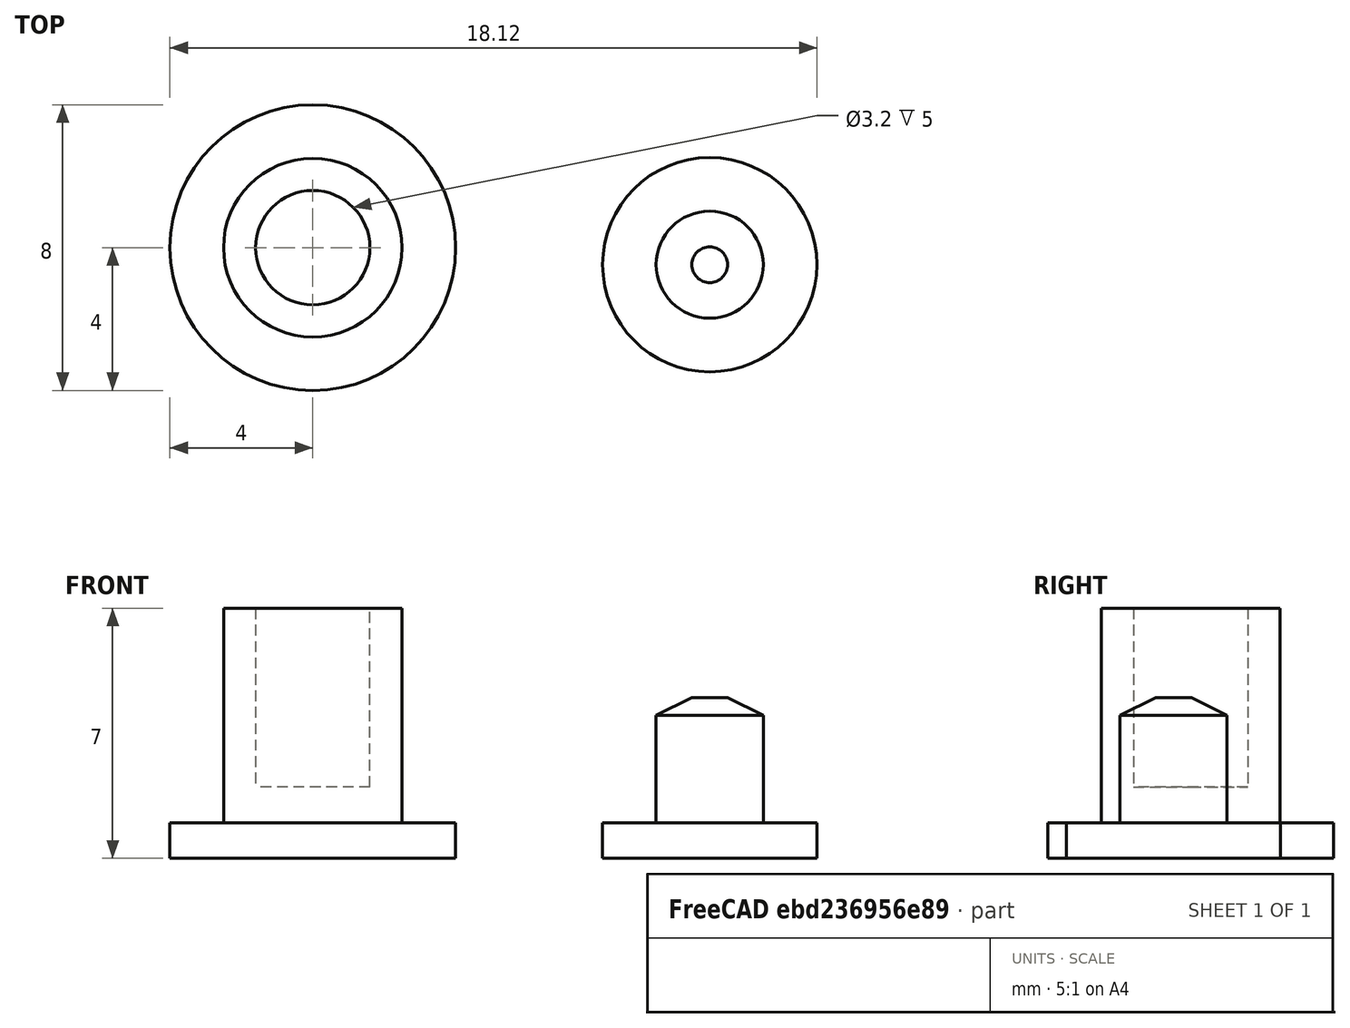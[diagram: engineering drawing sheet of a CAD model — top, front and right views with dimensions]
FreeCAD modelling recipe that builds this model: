
FCSTD DOCUMENT  (FreeCAD 0.20R29177 +426 (Git))
Label: planisphere
License: All rights reserved
LicenseURL: http://en.wikipedia.org/wiki/All_rights_reserved
objects: Part::Cylinder×5, Part::MultiFuse×3, Part::Cone×1, Part::Cut×1
note: 10 computed .brp shape members not serialized (recipe doc carries the construction recipe); baked Part::Feature solids carry a one-line shape summary decoded from their .brp

FEATURE [Part::Cylinder] Cylinder
  Angle = 360
  AttacherType = Attacher::AttachEngine3D
  FirstAngle = 0
  Height = 6
  Radius = 2.5
  SecondAngle = 0
FEATURE [Part::Cylinder] Cylinder001
  Angle = 360
  AttacherType = Attacher::AttachEngine3D
  FirstAngle = 0
  Height = 1
  Placement = pos=(0,1e-16,-1) rot=(0,0,1;0rad)
  Radius = 4
  SecondAngle = 0
FEATURE [Part::Cylinder] Cylinder002
  Angle = 360
  AttacherType = Attacher::AttachEngine3D
  FirstAngle = 0
  Height = 5
  Placement = pos=(0,0,1) rot=(0,0,1;0rad)
  Radius = 1.6
  SecondAngle = 0
FEATURE [Part::Cylinder] Cylinder003
  Angle = 360
  AttacherType = Attacher::AttachEngine3D
  FirstAngle = 0
  Height = 3
  Placement = pos=(11.1152,-0.477186,0) rot=(0,0,1;0rad)
  Radius = 1.5
  SecondAngle = 0
FEATURE [Part::Cylinder] Cylinder004
  Angle = 360
  AttacherType = Attacher::AttachEngine3D
  FirstAngle = 0
  Height = 1
  Placement = pos=(11.1152,-0.477186,-1) rot=(0,0,1;0rad)
  Radius = 3
  SecondAngle = 0
FEATURE [Part::Cone] Cone
  Angle = 360
  AttacherType = Attacher::AttachEngine3D
  Height = 0.5
  Placement = pos=(11.1152,-0.477186,3) rot=(0,0,1;0rad)
  Radius1 = 1.5
  Radius2 = 0.5
FEATURE [Part::Cut] Cut
  Base = -> Cylinder
  Tool = -> Cylinder002
FEATURE [Part::MultiFuse] Fusion
  Shapes = -> [Cylinder004,Cylinder003]
FEATURE [Part::MultiFuse] Fusion001
  Shapes = -> [Fusion,Cone]
FEATURE [Part::MultiFuse] Fusion002
  Shapes = -> [Cut,Cylinder001]
